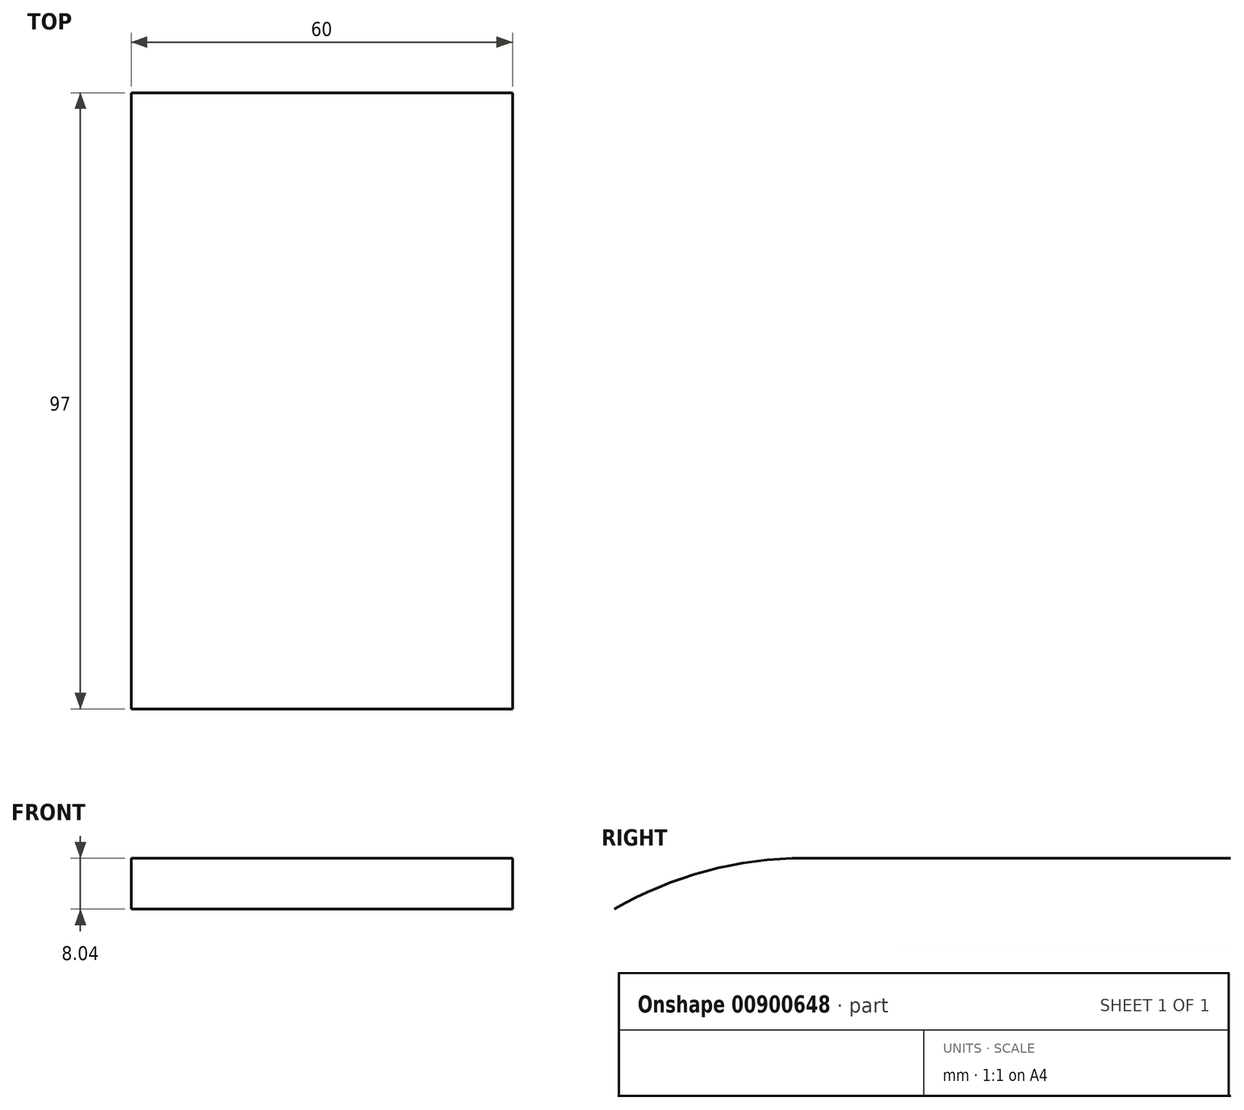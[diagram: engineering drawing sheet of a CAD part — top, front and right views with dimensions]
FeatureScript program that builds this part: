
annotation { "Feature Type Name" : "Feature", "Feature Type Description" : "" }
export const myFeature = defineFeature(function(context is Context, id is Id, definition is map)
    precondition{}
    {
        {
            var Q0;
            Q0=qCreatedBy(makeId("Front.planeOp"),FACE);
            var sketch = newSketch(context, id + "F0", { "sketchPlane" : qUnion([Q0])});
            skLineSegment(sketch, "E0.bottom", {"start": v(-30, -30) * mm, "end": v(30, -30) * mm});
            skLineSegment(sketch, "E0.top", {"start": v(-30, 30) * mm, "end": v(30, 30) * mm});
            skLineSegment(sketch, "E0.left", {"start": v(-30, -30) * mm, "end": v(-30, 30) * mm});
            skLineSegment(sketch, "E0.right", {"start": v(30, -30) * mm, "end": v(30, 30) * mm});
            skPoint(sketch, "E0.middle", {"position": v(0, 0) * mm});
            skSolve(sketch);
        }
        {
            var Q0;
            Q0=sQuery(id+"F0.wireOp",EDGE,"E0.top");
            extrude(context, id + "F1", {"bodyType" : ToolBodyType.SURFACE, "surfaceEntities" : qUnion([Q0]), "oppositeDirection" : true, "depth" : 67 * mm, "offsetDistance" : 25 * mm});
        }
        {
            var Q0;
            Q0=sQuery(id+"F0.wireOp",EDGE,"E0.top");
            var Q1;
            Q1=sQuery(id+"F0.wireOp",EDGE,"E0.bottom");
            revolve(context, id + "F2", {"bodyType" : ToolBodyType.SURFACE, "surfaceOperationType" : NewSurfaceOperationType.ADD, "surfaceEntities" : qUnion([Q0]), "axis" : qUnion([Q1]), "revolveType" : RevolveType.ONE_DIRECTION, "angle" : 30 * degree});
        }
    });
